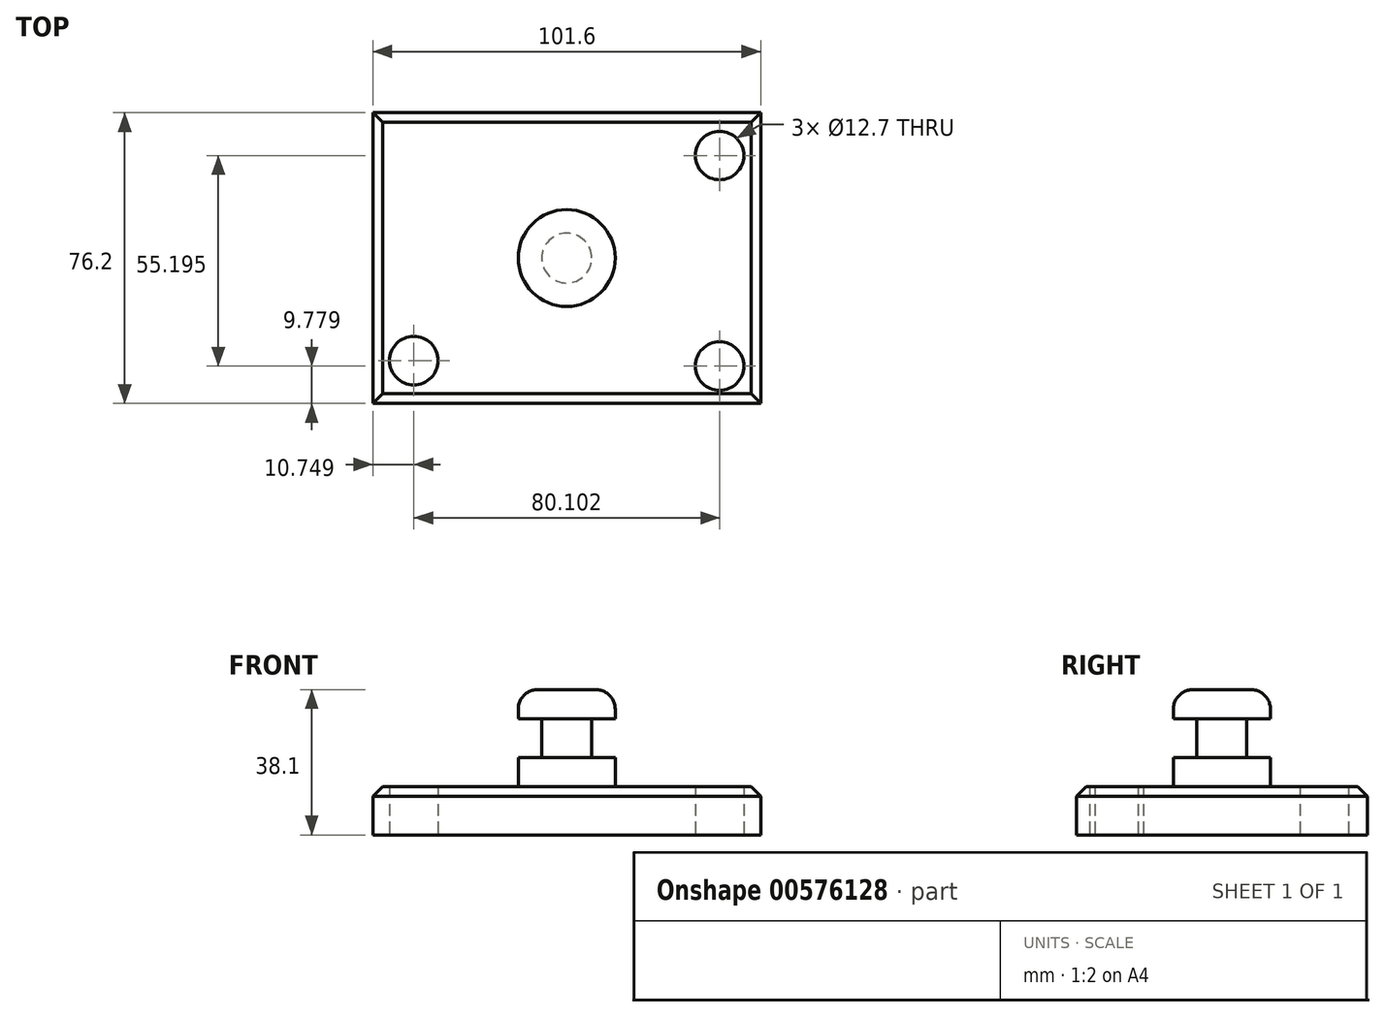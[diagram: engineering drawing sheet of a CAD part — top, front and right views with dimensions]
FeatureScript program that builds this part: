
annotation { "Feature Type Name" : "Feature", "Feature Type Description" : "" }
export const myFeature = defineFeature(function(context is Context, id is Id, definition is map)
    precondition{}
    {
        {
            var Q0;
            Q0=qCreatedBy(makeId("Top.planeOp"),FACE);
            var sketch = newSketch(context, id + "F0", { "sketchPlane" : qUnion([Q0])});
            skLineSegment(sketch, "E0.bottom", {"start": v(-50.8, -38.1) * mm, "end": v(50.8, -38.1) * mm});
            skLineSegment(sketch, "E0.top", {"start": v(-50.8, 38.1) * mm, "end": v(50.8, 38.1) * mm});
            skLineSegment(sketch, "E0.left", {"start": v(-50.8, -38.1) * mm, "end": v(-50.8, 38.1) * mm});
            skLineSegment(sketch, "E0.right", {"start": v(50.8, -38.1) * mm, "end": v(50.8, 38.1) * mm});
            skPoint(sketch, "E0.middle", {"position": v(0, 0) * mm});
            skSolve(sketch);
        }
        {
            var Q0;
            Q0=makeQuery(id+"F0.imprint","IMPRINT",FACE,{"disambiguationData":[TD([[makeQuery(id+"F0.imprint","IMPRINT",EDGE,{"derivedFrom":sQuery(id+"F0.wireOp",EDGE,"E0.bottom")}),1.0]])]});
            extrude(context, id + "F1", {"entities" : qUnion([Q0]), "depth" : 12.7 * mm, "offsetDistance" : 25.4 * mm});
        }
        {
            var Q0;
            Q0=qCreatedBy(makeId("Top.planeOp"),FACE);
            var sketch = newSketch(context, id + "F2", { "sketchPlane" : qUnion([Q0])});
            skCircle(sketch, "E1", {"center": v(-40.05, -26.87) * mm, "radius": 6.35 * mm});
            skCircle(sketch, "E2.MirrorC", {"center": v(-40.05, 26.87) * mm, "radius": 6.35 * mm});
            skCircle(sketch, "E3.MirrorC", {"center": v(40.05, 26.87) * mm, "radius": 6.35 * mm});
            skCircle(sketch, "E4", {"center": v(40.05, -28.32) * mm, "radius": 6.35 * mm});
            skSolve(sketch);
        }
        {
            var Q0;
            Q0=makeQuery(id+"F2.imprint","IMPRINT",FACE,{"disambiguationData":[TD([[makeQuery(id+"F2.imprint","IMPRINT",EDGE,{"derivedFrom":sQuery(id+"F2.wireOp",EDGE,"E4")}),1.0]])]});
            var Q1;
            Q1=makeQuery(id+"F2.imprint","IMPRINT",FACE,{"disambiguationData":[TD([[makeQuery(id+"F2.imprint","IMPRINT",EDGE,{"derivedFrom":sQuery(id+"F2.wireOp",EDGE,"E1")}),1.0]])]});
            var Q2;
            Q2=makeQuery(id+"F2.imprint","IMPRINT",FACE,{"disambiguationData":[TD([[makeQuery(id+"F2.imprint","IMPRINT",EDGE,{"derivedFrom":sQuery(id+"F2.wireOp",EDGE,"E2.MirrorC")}),-1.0]])]});
            var Q3;
            Q3=makeQuery(id+"F2.imprint","IMPRINT",FACE,{"disambiguationData":[TD([[makeQuery(id+"F2.imprint","IMPRINT",EDGE,{"derivedFrom":sQuery(id+"F2.wireOp",EDGE,"E3.MirrorC")}),1.0]])]});
            extrude(context, id + "F3", {"entities" : qUnion([Q0, Q1, Q2, Q3]), "operationType" : NewBodyOperationType.REMOVE, "endBound" : BoundingType.THROUGH_ALL, "depth" : 25.4 * mm, "offsetDistance" : 25.4 * mm});
        }
        {
            var Q0;
            Q0=qCreatedBy(makeId("Front.planeOp"),FACE);
            var sketch = newSketch(context, id + "F4", { "sketchPlane" : qUnion([Q0])});
            skLineSegment(sketch, "E5.bottom", {"start": v(0, 38.1) * mm, "end": v(12.7, 38.1) * mm});
            skLineSegment(sketch, "E5.top", {"start": v(0, 12.7) * mm, "end": v(12.7, 12.7) * mm});
            skLineSegment(sketch, "E5.left", {"start": v(0, 38.1) * mm, "end": v(0, 12.7) * mm});
            skLineSegment(sketch, "E5.right", {"start": v(12.7, 38.1) * mm, "end": v(12.7, 12.7) * mm});
            skSolve(sketch);
        }
        {
            var Q0;
            Q0=makeQuery(id+"F4.imprint","IMPRINT",FACE,{"disambiguationData":[TD([[makeQuery(id+"F4.imprint","IMPRINT",EDGE,{"derivedFrom":sQuery(id+"F4.wireOp",EDGE,"E5.bottom")}),-1.0]])]});
            var Q1;
            Q1=sQuery(id+"F4.wireOp",EDGE,"E5.left");
            revolve(context, id + "F5", {"operationType" : NewBodyOperationType.ADD, "entities" : qUnion([Q0]), "axis" : qUnion([Q1]), "revolveType" : RevolveType.FULL});
        }
        {
            var Q0;
            Q0=qCreatedBy(makeId("Front.planeOp"),FACE);
            var sketch = newSketch(context, id + "F6", { "sketchPlane" : qUnion([Q0])});
            skLineSegment(sketch, "E6.bottom", {"start": v(14.15, 30.49) * mm, "end": v(6.53, 30.49) * mm});
            skLineSegment(sketch, "E6.top", {"start": v(14.15, 20.33) * mm, "end": v(6.53, 20.33) * mm});
            skLineSegment(sketch, "E6.left", {"start": v(14.15, 30.49) * mm, "end": v(14.15, 20.33) * mm});
            skLineSegment(sketch, "E6.right", {"start": v(6.53, 30.49) * mm, "end": v(6.53, 20.33) * mm});
            skLineSegment(sketch, "E7", {"start": v(0, 16.52) * mm, "end": v(0, 49.38) * mm});
            skSolve(sketch);
        }
        {
            var Q0;
            Q0=makeQuery(id+"F6.imprint","IMPRINT",FACE,{"disambiguationData":[TD([[makeQuery(id+"F6.imprint","IMPRINT",EDGE,{"derivedFrom":sQuery(id+"F6.wireOp",EDGE,"E6.bottom")}),1.0]])]});
            var Q1;
            Q1=sQuery(id+"F6.wireOp",EDGE,"E7");
            revolve(context, id + "F7", {"operationType" : NewBodyOperationType.REMOVE, "entities" : qUnion([Q0]), "axis" : qUnion([Q1]), "revolveType" : RevolveType.FULL, "oppositeDirection" : true});
        }
        {
            var Q0;
            Q0=makeQuery(id+"F5.opRevolve","SWEPT_EDGE",EDGE,{"disambiguationData":[OSD([sQuery(id+"F4.wireOp",EDGE,"E5.bottom"),sQuery(id+"F4.wireOp",EDGE,"E5.right")])]});
            var Q1;
            Q1=makeQuery(id+"F5.opRevolve","SWEPT_EDGE",EDGE,{"disambiguationData":[OSD([sQuery(id+"F4.wireOp",EDGE,"E5.top"),sQuery(id+"F4.wireOp",EDGE,"E5.right")])]});
            fillet(context, id + "F8", {"entities" : qUnion([Q0, Q1]), "radius" : 5.08 * mm, "tangentPropagation" : true, "allowEdgeOverflow" : false});
        }
        {
            var Q0;
            Q0=makeQuery(id+"F1.opExtrude","CAP_EDGE",EDGE,{"disambiguationData":[OSD([sQuery(id+"F0.wireOp",EDGE,"E0.bottom")])],"isStart":false});
            var Q1;
            Q1=makeQuery(id+"F1.opExtrude","CAP_EDGE",EDGE,{"disambiguationData":[OSD([sQuery(id+"F0.wireOp",EDGE,"E0.right")])],"isStart":false});
            var Q2;
            Q2=makeQuery(id+"F1.opExtrude","CAP_EDGE",EDGE,{"disambiguationData":[OSD([sQuery(id+"F0.wireOp",EDGE,"E0.top")])],"isStart":false});
            var Q3;
            Q3=makeQuery(id+"F1.opExtrude","CAP_EDGE",EDGE,{"disambiguationData":[OSD([sQuery(id+"F0.wireOp",EDGE,"E0.left")])],"isStart":false});
            chamfer(context, id + "F9", {"entities" : qUnion([Q0, Q1, Q2, Q3]), "width" : 2.54 * mm, "tangentPropagation" : true});
        }
    });
